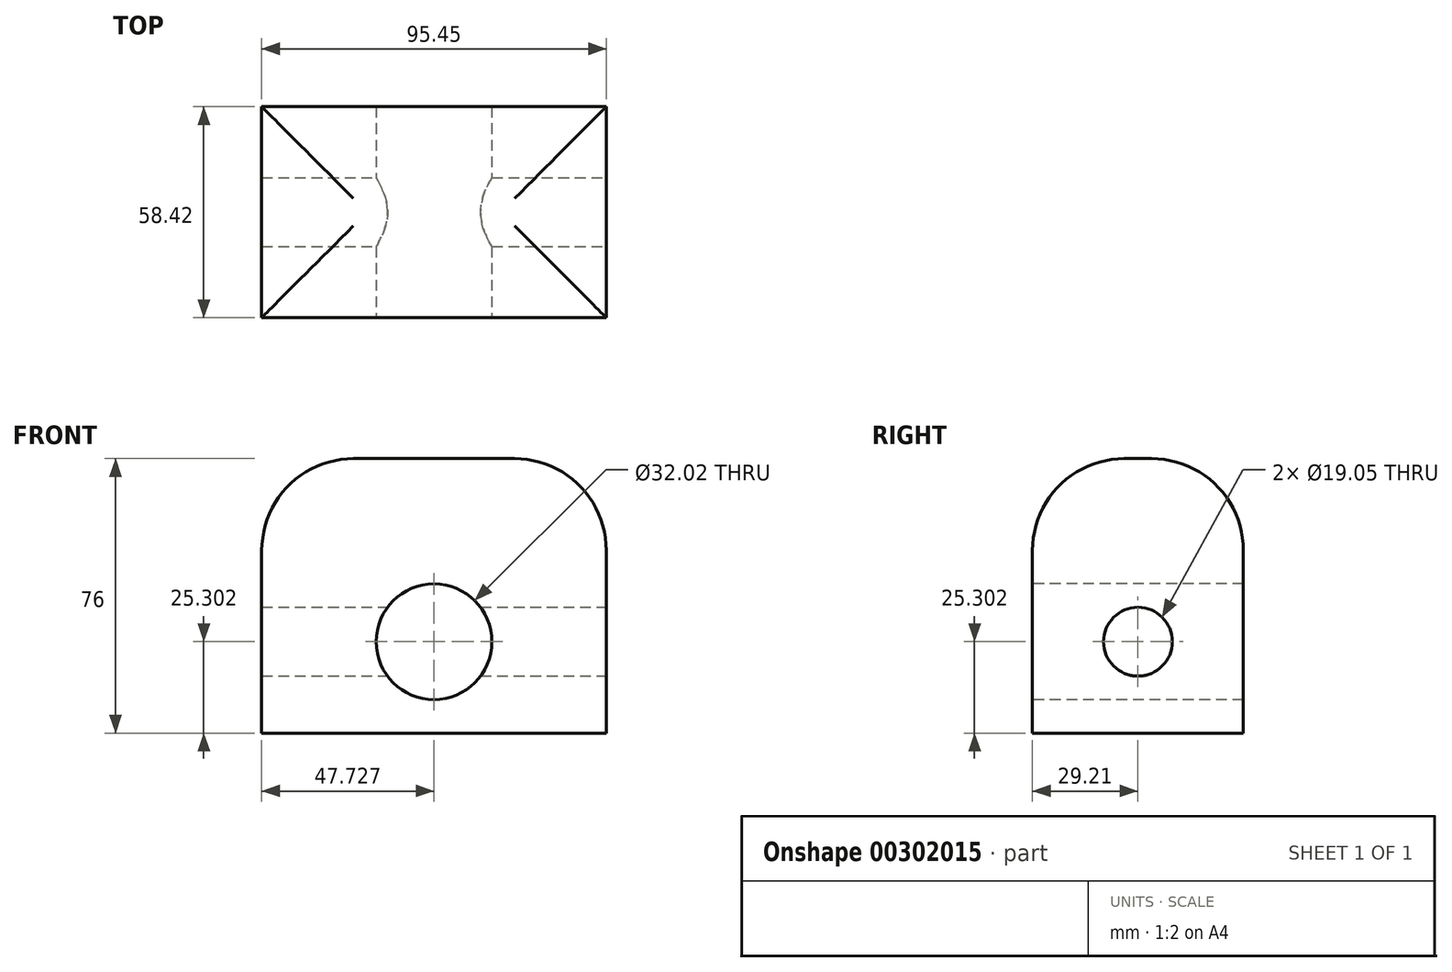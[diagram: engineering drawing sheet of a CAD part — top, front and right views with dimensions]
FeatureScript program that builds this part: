
annotation { "Feature Type Name" : "Feature", "Feature Type Description" : "" }
export const myFeature = defineFeature(function(context is Context, id is Id, definition is map)
    precondition{}
    {
        {
            var Q0;
            Q0=qCreatedBy(makeId("Front.planeOp"),FACE);
            var sketch = newSketch(context, id + "F0", { "sketchPlane" : qUnion([Q0])});
            skLineSegment(sketch, "E0.bottom", {"start": v(-48.93, 38.9) * mm, "end": v(46.52, 38.9) * mm});
            skLineSegment(sketch, "E0.top", {"start": v(-48.93, -37.1) * mm, "end": v(46.52, -37.1) * mm});
            skLineSegment(sketch, "E0.left", {"start": v(-48.93, 38.9) * mm, "end": v(-48.93, -37.1) * mm});
            skLineSegment(sketch, "E0.right", {"start": v(46.52, 38.9) * mm, "end": v(46.52, -37.1) * mm});
            skSolve(sketch);
        }
        {
            var Q0;
            Q0 = qSketchRegion(id + "F0", true);
            extrude(context, id + "F1", {"entities" : qUnion([Q0]), "depth" : 58.42 * mm});
        }
        {
            var Q0;
            Q0=makeQuery(id+"F1.opExtrude","CAP_EDGE",EDGE,{"disambiguationData":[OSD([sQuery(id+"F0.wireOp",EDGE,"E0.bottom")])],"isStart":false});
            var Q1;
            Q1=makeQuery(id+"F1.opExtrude","SWEPT_EDGE",EDGE,{"disambiguationData":[OSD([sQuery(id+"F0.wireOp",EDGE,"E0.bottom"),sQuery(id+"F0.wireOp",EDGE,"E0.right")])]});
            var Q2;
            Q2=makeQuery(id+"F1.opExtrude","SWEPT_EDGE",EDGE,{"disambiguationData":[OSD([sQuery(id+"F0.wireOp",EDGE,"E0.bottom"),sQuery(id+"F0.wireOp",EDGE,"E0.left")])]});
            var Q3;
            Q3=makeQuery(id+"F1.opExtrude","CAP_EDGE",EDGE,{"disambiguationData":[OSD([sQuery(id+"F0.wireOp",EDGE,"E0.bottom")])],"isStart":true});
            fillet(context, id + "F2", {"entities" : qUnion([Q0, Q1, Q2, Q3]), "radius" : 25.4 * mm, "tangentPropagation" : true, "allowEdgeOverflow" : false});
        }
        {
            var Q0;
            Q0=makeQuery(id+"F1.opExtrude","CAP_FACE",FACE,{"disambiguationData":[OSD([sQuery(id+"F0.wireOp",EDGE,"E0.bottom"),sQuery(id+"F0.wireOp",EDGE,"E0.top"),sQuery(id+"F0.wireOp",EDGE,"E0.left"),sQuery(id+"F0.wireOp",EDGE,"E0.right")])],"isStart":false});
            var sketch = newSketch(context, id + "F3", { "sketchPlane" : qUnion([Q0])});
            skCircle(sketch, "E1", {"center": v(-1.2, -11.8) * mm, "radius": 16 * mm});
            skPoint(sketch, "E1.centerSnap0", {"position": v(46.52, -11.8) * mm});
            skPoint(sketch, "E1.centerSnap1", {"position": v(-1.2, -37.1) * mm});
            skSolve(sketch);
        }
        {
            var Q0;
            Q0 = qSketchRegion(id + "F3", true);
            extrude(context, id + "F4", {"entities" : qUnion([Q0]), "operationType" : NewBodyOperationType.REMOVE, "endBound" : BoundingType.THROUGH_ALL, "oppositeDirection" : true, "depth" : 25.4 * mm});
        }
        {
            var Q0;
            Q0=makeQuery(id+"F1.opExtrude","SWEPT_FACE",FACE,{"disambiguationData":[OSD([sQuery(id+"F0.wireOp",EDGE,"E0.right")])]});
            var sketch = newSketch(context, id + "F5", { "sketchPlane" : qUnion([Q0])});
            skPoint(sketch, "E2", {"position": v(-29.21, -11.8) * mm});
            skPoint(sketch, "E2.positionSnap0", {"position": v(-29.21, 13.5) * mm});
            skPoint(sketch, "E2.positionSnap1", {"position": v(0, -11.8) * mm});
            skSolve(sketch);
        }
        {
            var Q0;
            Q0=sQuery(id+"F5.wireOp",VERTEX,"E2");
            var Q1;
            Q1=makeQuery(id+"F1.opExtrude","SWEPT_BODY",BODY,{"disambiguationData":[OSD([sQuery(id+"F0.wireOp",EDGE,"E0.bottom"),sQuery(id+"F0.wireOp",EDGE,"E0.top"),sQuery(id+"F0.wireOp",EDGE,"E0.left"),sQuery(id+"F0.wireOp",EDGE,"E0.right")])]});
            hole(context, id + "F6", {"style" : HoleStyle.SIMPLE, "endStyle" : HoleEndStyle.THROUGH, "holeDiameter" : 19.05 * mm, "tappedDepth" : 12.7 * mm, "tapClearance" : 3, "locations" : qUnion([Q0]), "scope" : qUnion([Q1])});
        }
    });
